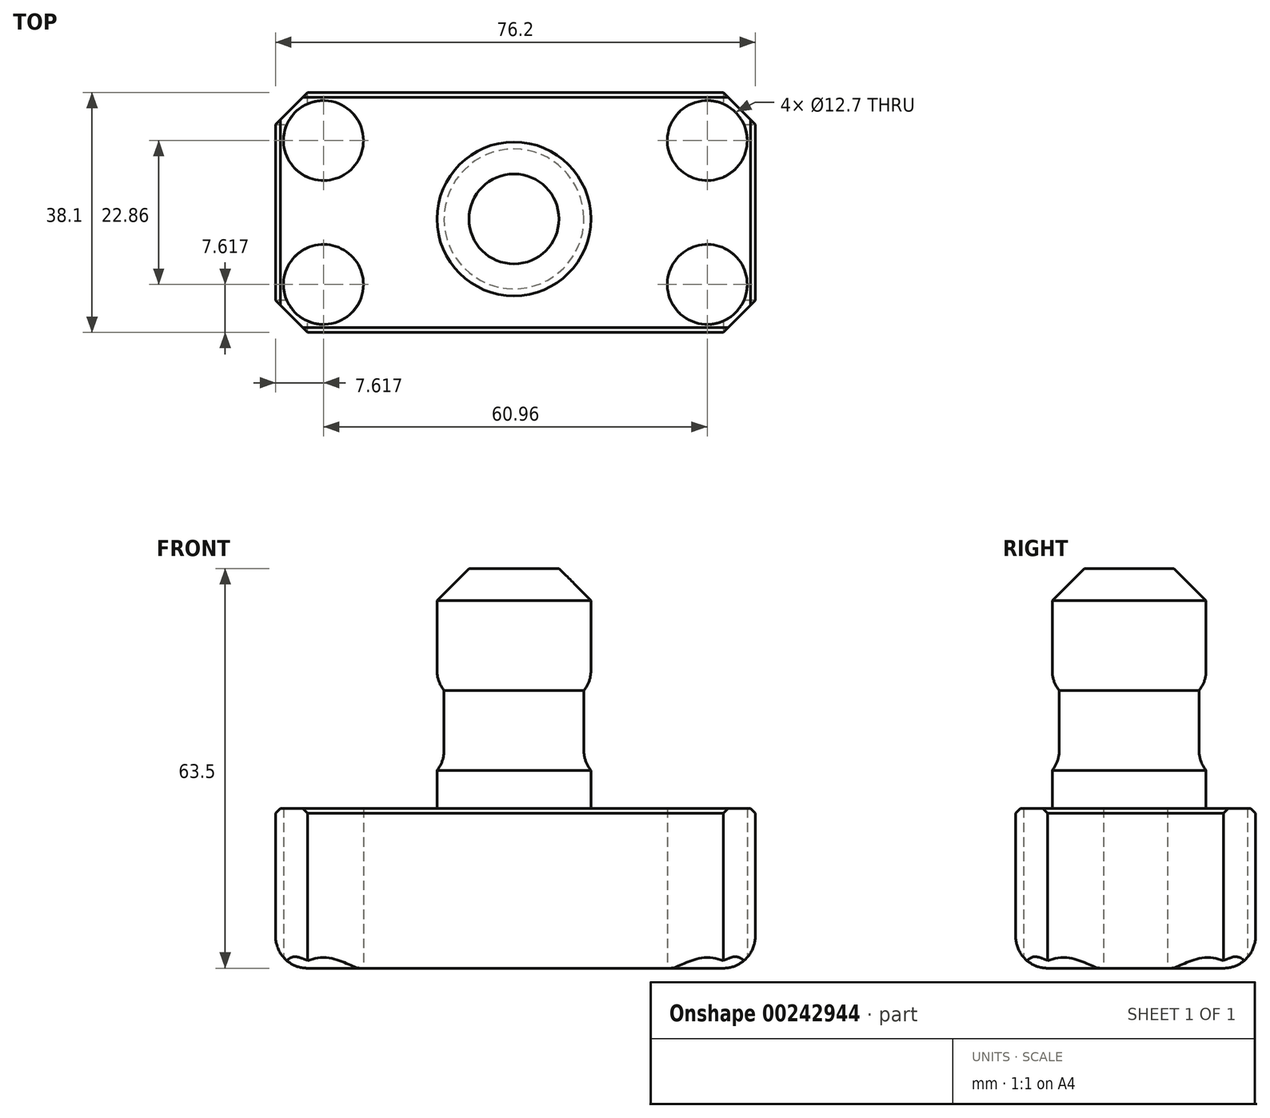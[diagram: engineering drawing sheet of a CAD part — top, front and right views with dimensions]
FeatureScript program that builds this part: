
annotation { "Feature Type Name" : "Feature", "Feature Type Description" : "" }
export const myFeature = defineFeature(function(context is Context, id is Id, definition is map)
    precondition{}
    {
        {
            var Q0;
            Q0=qCreatedBy(makeId("Top.planeOp"),FACE);
            var sketch = newSketch(context, id + "F0", { "sketchPlane" : qUnion([Q0])});
            skLineSegment(sketch, "E0.bottom", {"start": v(-28.7, 26.34) * mm, "end": v(47.5, 26.34) * mm});
            skLineSegment(sketch, "E0.top", {"start": v(-28.7, -11.76) * mm, "end": v(47.5, -11.76) * mm});
            skLineSegment(sketch, "E0.left", {"start": v(-28.7, 26.34) * mm, "end": v(-28.7, -11.76) * mm});
            skLineSegment(sketch, "E0.right", {"start": v(47.5, 26.34) * mm, "end": v(47.5, -11.76) * mm});
            skSolve(sketch);
        }
        {
            var Q0;
            Q0 = qSketchRegion(id + "F0", true);
            extrude(context, id + "F1", {"entities" : qUnion([Q0]), "depth" : 25.4 * mm});
        }
        {
            var Q0;
            Q0=qCreatedBy(makeId("Top.planeOp"),FACE);
            var sketch = newSketch(context, id + "F2", { "sketchPlane" : qUnion([Q0])});
            skCircle(sketch, "E1", {"center": v(-21.08, 18.72) * mm, "radius": 6.35 * mm});
            skSolve(sketch);
        }
        {
            var Q0;
            Q0=qCreatedBy(makeId("Top.planeOp"),FACE);
            var sketch = newSketch(context, id + "F3", { "sketchPlane" : qUnion([Q0])});
            skSolve(sketch);
        }
        {
            var Q0;
            Q0 = qSketchRegion(id + "F3", true);
            var Q1;
            Q1 = qSketchRegion(id + "F2", true);
            extrude(context, id + "F4", {"entities" : qUnion([Q0, Q1]), "operationType" : NewBodyOperationType.REMOVE, "depth" : 25.4 * mm});
        }
        {
            var Q0;
            Q0=qCreatedBy(makeId("Top.planeOp"),FACE);
            var sketch = newSketch(context, id + "F5", { "sketchPlane" : qUnion([Q0])});
            skCircle(sketch, "E2", {"center": v(39.88, 18.72) * mm, "radius": 6.35 * mm});
            skSolve(sketch);
        }
        {
            var Q0;
            Q0 = qSketchRegion(id + "F5", true);
            extrude(context, id + "F6", {"entities" : qUnion([Q0]), "operationType" : NewBodyOperationType.REMOVE, "depth" : 25.4 * mm});
        }
        {
            var Q0;
            Q0=qCreatedBy(makeId("Top.planeOp"),FACE);
            var sketch = newSketch(context, id + "F7", { "sketchPlane" : qUnion([Q0])});
            skCircle(sketch, "E3", {"center": v(-21.08, -4.14) * mm, "radius": 6.35 * mm});
            skSolve(sketch);
        }
        {
            var Q0;
            Q0 = qSketchRegion(id + "F7", true);
            extrude(context, id + "F8", {"entities" : qUnion([Q0]), "operationType" : NewBodyOperationType.REMOVE, "depth" : 25.4 * mm});
        }
        {
            var Q0;
            Q0=qCreatedBy(makeId("Top.planeOp"),FACE);
            var sketch = newSketch(context, id + "F9", { "sketchPlane" : qUnion([Q0])});
            skCircle(sketch, "E4", {"center": v(39.88, -4.14) * mm, "radius": 6.35 * mm});
            skSolve(sketch);
        }
        {
            var Q0;
            Q0 = qSketchRegion(id + "F9", true);
            extrude(context, id + "F10", {"entities" : qUnion([Q0]), "operationType" : NewBodyOperationType.REMOVE, "depth" : 25.4 * mm});
        }
        {
            var Q0;
            Q0=makeQuery(id+"F1.opExtrude","CAP_FACE",FACE,{"disambiguationData":[OSD([sQuery(id+"F0.wireOp",EDGE,"E0.bottom"),sQuery(id+"F0.wireOp",EDGE,"E0.top"),sQuery(id+"F0.wireOp",EDGE,"E0.left"),sQuery(id+"F0.wireOp",EDGE,"E0.right")])],"isStart":false});
            var sketch = newSketch(context, id + "F11", { "sketchPlane" : qUnion([Q0])});
            skCircle(sketch, "E5", {"center": v(9.17, 6.26) * mm, "radius": 12.22 * mm});
            skSolve(sketch);
        }
        {
            var Q0;
            Q0 = qSketchRegion(id + "F11", true);
            extrude(context, id + "F12", {"entities" : qUnion([Q0]), "operationType" : NewBodyOperationType.ADD, "depth" : 38.1 * mm});
        }
        {
            var Q0;
            Q0=qCreatedBy(makeId("Front.planeOp"),FACE);
            var sketch = newSketch(context, id + "F13", { "sketchPlane" : qUnion([Q0])});
            skLineSegment(sketch, "E6.bottom", {"start": v(-12.7, 44.1) * mm, "end": v(0, 44.1) * mm});
            skLineSegment(sketch, "E6.top", {"start": v(-12.7, 31.4) * mm, "end": v(0, 31.4) * mm});
            skLineSegment(sketch, "E6.left", {"start": v(-12.7, 44.1) * mm, "end": v(-12.7, 31.4) * mm});
            skLineSegment(sketch, "E6.right", {"start": v(0, 44.1) * mm, "end": v(0, 31.4) * mm});
            skSolve(sketch);
        }
        {
            var Q0;
            Q0 = qSketchRegion(id + "F13", true);
            var Q1;
            Q1=makeQuery(id+"F12.opExtrude","SWEPT_FACE",FACE,{"disambiguationData":[OSD([sQuery(id+"F11.wireOp",EDGE,"E5")])]});
            revolve(context, id + "F14", {"operationType" : NewBodyOperationType.REMOVE, "entities" : qUnion([Q0]), "axis" : qUnion([Q1]), "revolveType" : RevolveType.FULL, "oppositeDirection" : true});
        }
        {
            var Q0;
            Q0=makeQuery(id+"F14.boolean.opBoolean","INTERSECT",EDGE,{"derivedFrom":[makeQuery(id+"F12.opExtrude","SWEPT_FACE",FACE,{"disambiguationData":[OSD([sQuery(id+"F11.wireOp",EDGE,"E5")])]}),makeQuery(id+"F14.opRevolve","SWEPT_FACE",FACE,{"disambiguationData":[OSD([sQuery(id+"F13.wireOp",EDGE,"E6.bottom")])]})]});
            fillet(context, id + "F15", {"entities" : qUnion([Q0]), "radius" : 5.08 * mm, "tangentPropagation" : true, "allowEdgeOverflow" : false});
        }
        {
            var Q0;
            Q0=makeQuery(id+"F14.boolean.opBoolean","COPY",EDGE,{"derivedFrom":makeQuery(id+"F14.opRevolve","SWEPT_EDGE",EDGE,{"disambiguationData":[OSD([sQuery(id+"F13.wireOp",EDGE,"E6.top"),sQuery(id+"F13.wireOp",EDGE,"E6.right")])]})});
            var Q1;
            Q1=makeQuery(id+"F12.opExtrude","CAP_EDGE",EDGE,{"disambiguationData":[OSD([sQuery(id+"F11.wireOp",EDGE,"E5")])],"isStart":true});
            fillet(context, id + "F16", {"entities" : qUnion([Q0, Q1]), "radius" : 5.08 * mm, "tangentPropagation" : true, "allowEdgeOverflow" : false});
        }
        {
            var Q0;
            Q0=makeQuery(id+"F1.opExtrude","CAP_EDGE",EDGE,{"disambiguationData":[OSD([sQuery(id+"F0.wireOp",EDGE,"E0.top")])],"isStart":false});
            var Q1;
            Q1=makeQuery(id+"F1.opExtrude","CAP_EDGE",EDGE,{"disambiguationData":[OSD([sQuery(id+"F0.wireOp",EDGE,"E0.left")])],"isStart":false});
            var Q2;
            Q2=makeQuery(id+"F1.opExtrude","CAP_EDGE",EDGE,{"disambiguationData":[OSD([sQuery(id+"F0.wireOp",EDGE,"E0.right")])],"isStart":false});
            var Q3;
            Q3=makeQuery(id+"F1.opExtrude","CAP_EDGE",EDGE,{"disambiguationData":[OSD([sQuery(id+"F0.wireOp",EDGE,"E0.bottom")])],"isStart":false});
            chamfer(context, id + "F17", {"entities" : qUnion([Q0, Q1, Q2, Q3]), "width" : 0.76 * mm, "tangentPropagation" : true});
        }
        {
            var Q0;
            Q0=makeQuery(id+"F1.opExtrude","CAP_EDGE",EDGE,{"disambiguationData":[OSD([sQuery(id+"F0.wireOp",EDGE,"E0.top")])],"isStart":true});
            var Q1;
            Q1=makeQuery(id+"F1.opExtrude","CAP_EDGE",EDGE,{"disambiguationData":[OSD([sQuery(id+"F0.wireOp",EDGE,"E0.right")])],"isStart":true});
            var Q2;
            Q2=makeQuery(id+"F1.opExtrude","CAP_EDGE",EDGE,{"disambiguationData":[OSD([sQuery(id+"F0.wireOp",EDGE,"E0.bottom")])],"isStart":true});
            var Q3;
            Q3=makeQuery(id+"F1.opExtrude","CAP_EDGE",EDGE,{"disambiguationData":[OSD([sQuery(id+"F0.wireOp",EDGE,"E0.left")])],"isStart":true});
            fillet(context, id + "F18", {"entities" : qUnion([Q0, Q1, Q2, Q3]), "radius" : 5.08 * mm, "tangentPropagation" : true, "allowEdgeOverflow" : false});
        }
        {
            var Q0;
            Q0=makeQuery(id+"F1.opExtrude","SWEPT_EDGE",EDGE,{"disambiguationData":[OSD([sQuery(id+"F0.wireOp",EDGE,"E0.top"),sQuery(id+"F0.wireOp",EDGE,"E0.right")])]});
            var Q1;
            Q1=makeQuery(id+"F1.opExtrude","SWEPT_EDGE",EDGE,{"disambiguationData":[OSD([sQuery(id+"F0.wireOp",EDGE,"E0.bottom"),sQuery(id+"F0.wireOp",EDGE,"E0.right")])]});
            var Q2;
            Q2=makeQuery(id+"F1.opExtrude","SWEPT_EDGE",EDGE,{"disambiguationData":[OSD([sQuery(id+"F0.wireOp",EDGE,"E0.bottom"),sQuery(id+"F0.wireOp",EDGE,"E0.left")])]});
            var Q3;
            Q3=makeQuery(id+"F1.opExtrude","SWEPT_EDGE",EDGE,{"disambiguationData":[OSD([sQuery(id+"F0.wireOp",EDGE,"E0.top"),sQuery(id+"F0.wireOp",EDGE,"E0.left")])]});
            chamfer(context, id + "F19", {"entities" : qUnion([Q0, Q1, Q2, Q3]), "width" : 5.08 * mm, "tangentPropagation" : true});
        }
        {
            var Q0;
            Q0=makeQuery(id+"F12.opExtrude","CAP_EDGE",EDGE,{"disambiguationData":[OSD([sQuery(id+"F11.wireOp",EDGE,"E5")])],"isStart":false});
            chamfer(context, id + "F20", {"entities" : qUnion([Q0]), "width" : 5.08 * mm, "tangentPropagation" : true});
        }
    });
